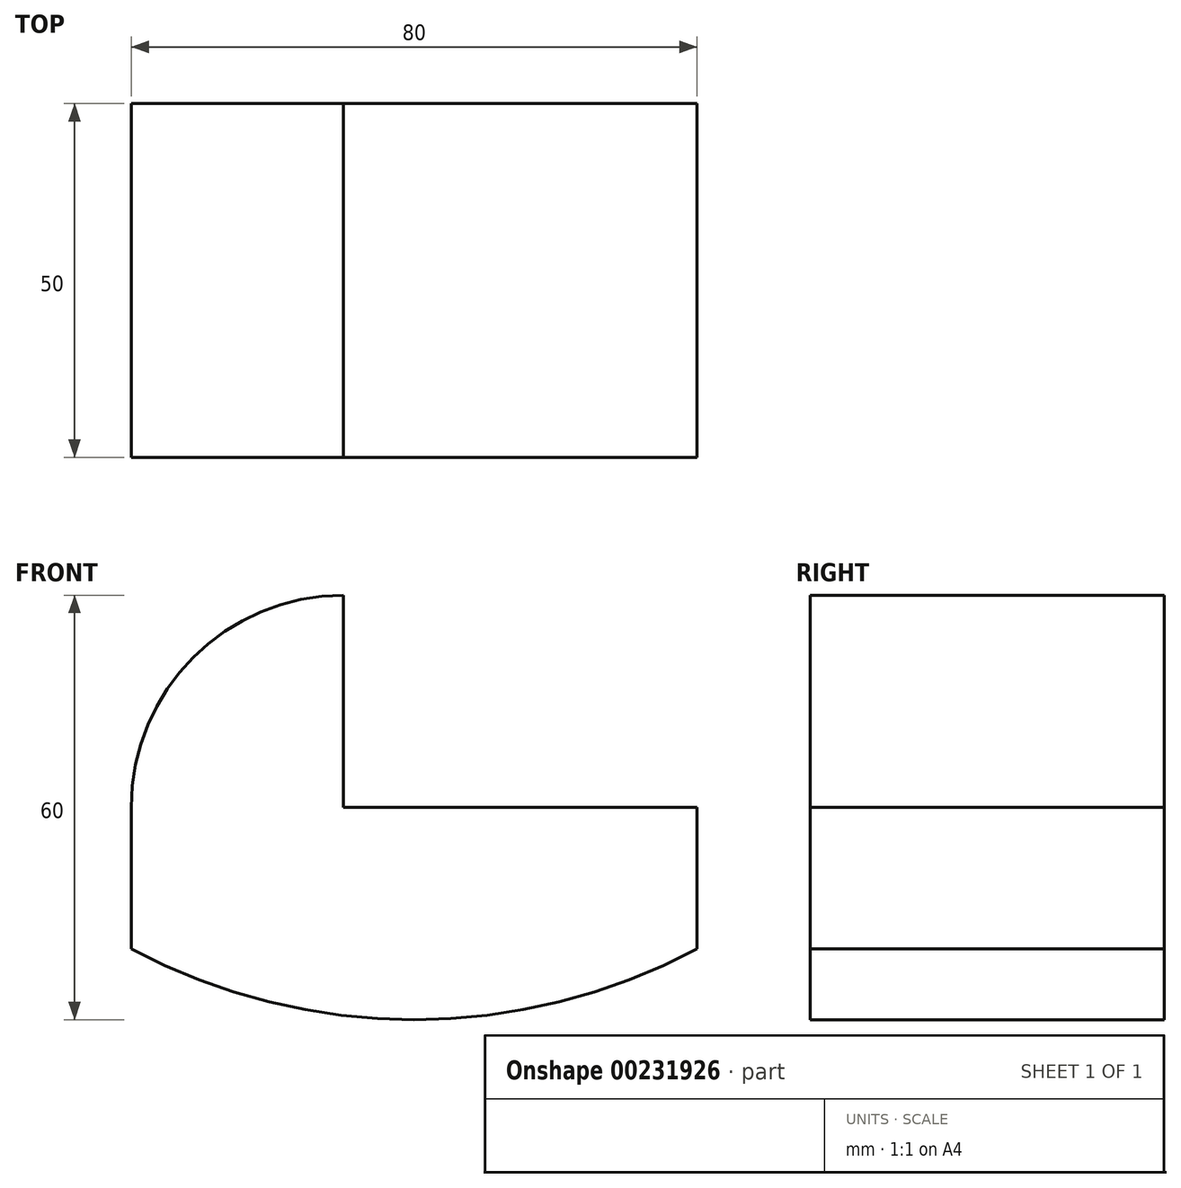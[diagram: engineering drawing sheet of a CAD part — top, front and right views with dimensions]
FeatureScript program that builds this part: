
annotation { "Feature Type Name" : "Feature", "Feature Type Description" : "" }
export const myFeature = defineFeature(function(context is Context, id is Id, definition is map)
    precondition{}
    {
        {
            var Q0;
            Q0=qCreatedBy(makeId("Front.planeOp"),FACE);
            var sketch = newSketch(context, id + "F0", { "sketchPlane" : qUnion([Q0])});
            skLineSegment(sketch, "E0", {"start": v(-50, 60) * mm, "end": v(-50, 30) * mm});
            skLineSegment(sketch, "E1", {"start": v(-50, 30) * mm, "end": v(0, 30) * mm});
            skArc(sketch, "E2", {"start": v(-50, 60) * mm, "mid": v(-71.21, 51.21) * mm, "end": v(-80, 30) * mm});
            skLineSegment(sketch, "E3", {"start": v(-80, 30) * mm, "end": v(-80, 10) * mm});
            skLineSegment(sketch, "E4", {"start": v(0, 30) * mm, "end": v(0, 10) * mm});
            skArc(sketch, "E5", {"start": v(-80, 10) * mm, "mid": v(-40, 0) * mm, "end": v(0, 10) * mm});
            skSolve(sketch);
        }
        {
            var Q0;
            Q0=makeQuery(id+"F0.imprint","IMPRINT",FACE,{"disambiguationData":[TD([[makeQuery(id+"F0.imprint","IMPRINT",EDGE,{"derivedFrom":sQuery(id+"F0.wireOp",EDGE,"E0")}),-1.0]])]});
            extrude(context, id + "F1", {"entities" : qUnion([Q0]), "depth" : 50 * mm});
        }
    });
